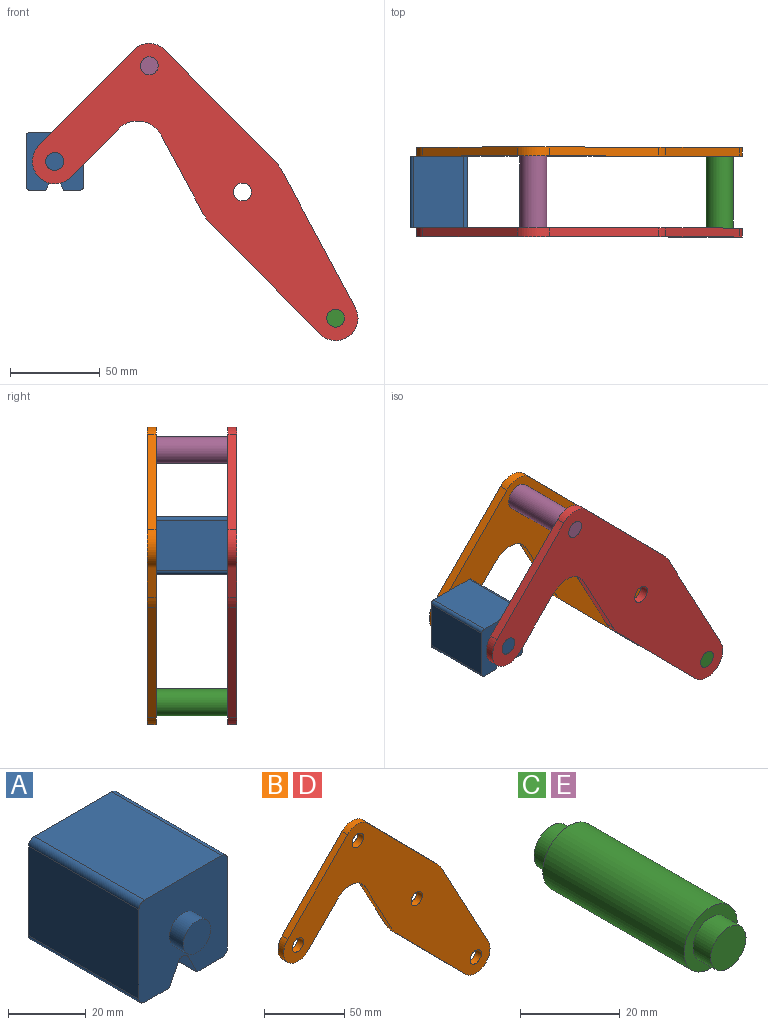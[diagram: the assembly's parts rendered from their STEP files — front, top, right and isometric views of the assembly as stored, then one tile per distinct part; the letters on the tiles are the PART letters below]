
ASSEMBLY  parts=5 mates=3
PART A: 18 faces, bbox 32.1x50x32.1 mm
  f0: plane 40x28.08mm, normal (1,0,0), area 1123.1mm2, adj f4,f10,f13,f14
  f1: plane 40x9.04mm, normal (0,0,-1), area 361.6mm2, adj f2,f4,f10,f14
  f2: plane 40x6.42mm, normal (-0.89,0,-0.45), area 287.2mm2, adj f1,f4,f10,f15
  f3: plane 40x6.42mm, normal (0.89,0,-0.45), area 287.2mm2, adj f4,f5,f10,f15
  f4: plane 32.08x32.08mm, normal (0,-1,0), area 900.6mm2, adj f0,f1,f2,f3,f5,f6,f7,f9
  f5: plane 40x9.04mm, normal (0,0,-1), area 361.6mm2, adj f3,f4,f10,f16
  f6: plane 40x28.08mm, normal (0,0,1), area 1123.1mm2, adj f4,f10,f13,f17
  f7: plane 40x28.08mm, normal (-1,0,0), area 1123.1mm2, adj f4,f10,f16,f17
  f8: plane 10x10mm, normal (0,-1,0), area 78.5mm2, adj f9
  f9: cylinder r=5mm len=10mm, axis (0,1,0), area 157.1mm2, adj f4,f8
  f10: plane 32.08x32.08mm, normal (0,1,0), area 900.6mm2, adj f0,f1,f2,f3,f5,f6,f7,f12
  f11: plane 10x10mm, normal (0,1,0), area 78.5mm2, adj f12
  f12: cylinder r=5mm len=10mm, axis (0,-1,0), area 157.1mm2, adj f10,f11
  f13: cylinder r=2mm len=40mm, axis (0,1,0), area 125.7mm2, adj f0,f4,f6,f10
  f14: cylinder r=2mm len=40mm, axis (0,-1,0), area 125.7mm2, adj f0,f1,f4,f10
  f15: cylinder r=2mm len=40mm, axis (0,1,0), area 177.1mm2, adj f2,f3,f4,f10
  f16: cylinder r=2mm len=40mm, axis (0,1,0), area 125.7mm2, adj f4,f5,f7,f10
  f17: cylinder r=2mm len=40mm, axis (0,-1,0), area 125.7mm2, adj f4,f6,f7,f10
PART B: 18 faces, bbox 181.7x5x165.8 mm
  f0: plane 43.49x23.35mm, normal (-0.88,0,-0.47), area 246.8mm2, adj f1,f14,f16,f17
  f1: cylinder r=25mm len=5.75mm, axis (0,1,0), area 35.8mm2, adj f0,f2,f16,f17
  f2: plane 61.6x60.87mm, normal (-0.71,0,-0.7), area 433mm2, adj f1,f3,f16,f17
  f3: cylinder r=12.5mm len=21.39mm, axis (0,1,0), area 178.4mm2, adj f2,f4,f16,f17
  f4: plane 76.3x40.96mm, normal (0.88,0,0.47), area 433mm2, adj f3,f5,f16,f17
  f5: cylinder r=25mm len=5.75mm, axis (0,1,0), area 35.8mm2, adj f4,f6,f16,f17
  f6: plane 61.6x60.87mm, normal (0.71,0,0.7), area 433mm2, adj f5,f7,f16,f17
  f7: cylinder r=12.5mm len=17.78mm, axis (0,1,0), area 98.9mm2, adj f6,f8,f16,f17
  f8: plane 53.35x52.71mm, normal (-0.71,0,0.7), area 375mm2, adj f7,f9,f16,f17
  f9: cylinder r=12.5mm len=21.39mm, axis (0,1,0), area 196.3mm2, adj f8,f10,f16,f17
  f10: plane 26.86x26.54mm, normal (0.71,0,-0.7), area 188.8mm2, adj f9,f14,f16,f17
  f11: cylinder r=5mm len=10mm, axis (0,1,0), area 157.1mm2, adj f16,f17
  f12: cylinder r=5mm len=10mm, axis (0,1,0), area 157.1mm2, adj f16,f17
  f13: cylinder r=5mm len=10mm, axis (0,1,0), area 157.1mm2, adj f16,f17
  f14: cylinder r=15mm len=23.89mm, axis (0,1,0), area 140.2mm2, adj f0,f10,f16,f17
  f15: cylinder r=5mm len=10mm, axis (0,1,0), area 157.1mm2, adj f16,f17
  f16: plane 181.66x165.78mm, normal (0,-1,0), area 8710.1mm2, adj f0,f1,f2,f3,f4,f5,f6,f7
  f17: plane 181.66x165.78mm, normal (0,1,0), area 8710.1mm2, adj f0,f1,f2,f3,f4,f5,f6,f7
PART C: 7 faces, bbox 15x50x15 mm
  f0: cylinder r=7.5mm len=40mm, axis (0,-1,0), area 1885mm2, adj f2,f5
  f1: cylinder r=5mm len=10mm, axis (0,1,0), area 157.1mm2, adj f2,f3
  f2: plane 15x15mm, normal (0,-1,0), area 98.2mm2, adj f0,f1
  f3: plane 10x10mm, normal (0,-1,0), area 78.5mm2, adj f1
  f4: cylinder r=5mm len=10mm, axis (0,-1,0), area 157.1mm2, adj f5,f6
  f5: plane 15x15mm, normal (0,1,0), area 98.2mm2, adj f0,f4
  f6: plane 10x10mm, normal (0,1,0), area 78.5mm2, adj f4
PART D: same geometry as B
PART E: same geometry as C
PLACE A t=(-29.07,-75.3,7.86)mm
PLACE B t=(-29.07,-30.3,7.86)mm
PLACE C t=(74.88,-75.3,-132.92)mm
PLACE D t=(-29.07,-75.3,7.86)mm fixed
PLACE E t=(-29.07,-75.3,7.86)mm
MATE fastened C.f0 <-> D.f3  axis (0,-1,0) through (22.91,-75.3,-62.53)mm
MATE fastened B.f7 <-> E.f0  axis (0,-1,0) through (-81.04,-35.3,78.25)mm
MATE revolute A.f9 <-> D.f9  axis (0,-1,0) through (-133.76,-75.3,24.9)mm
